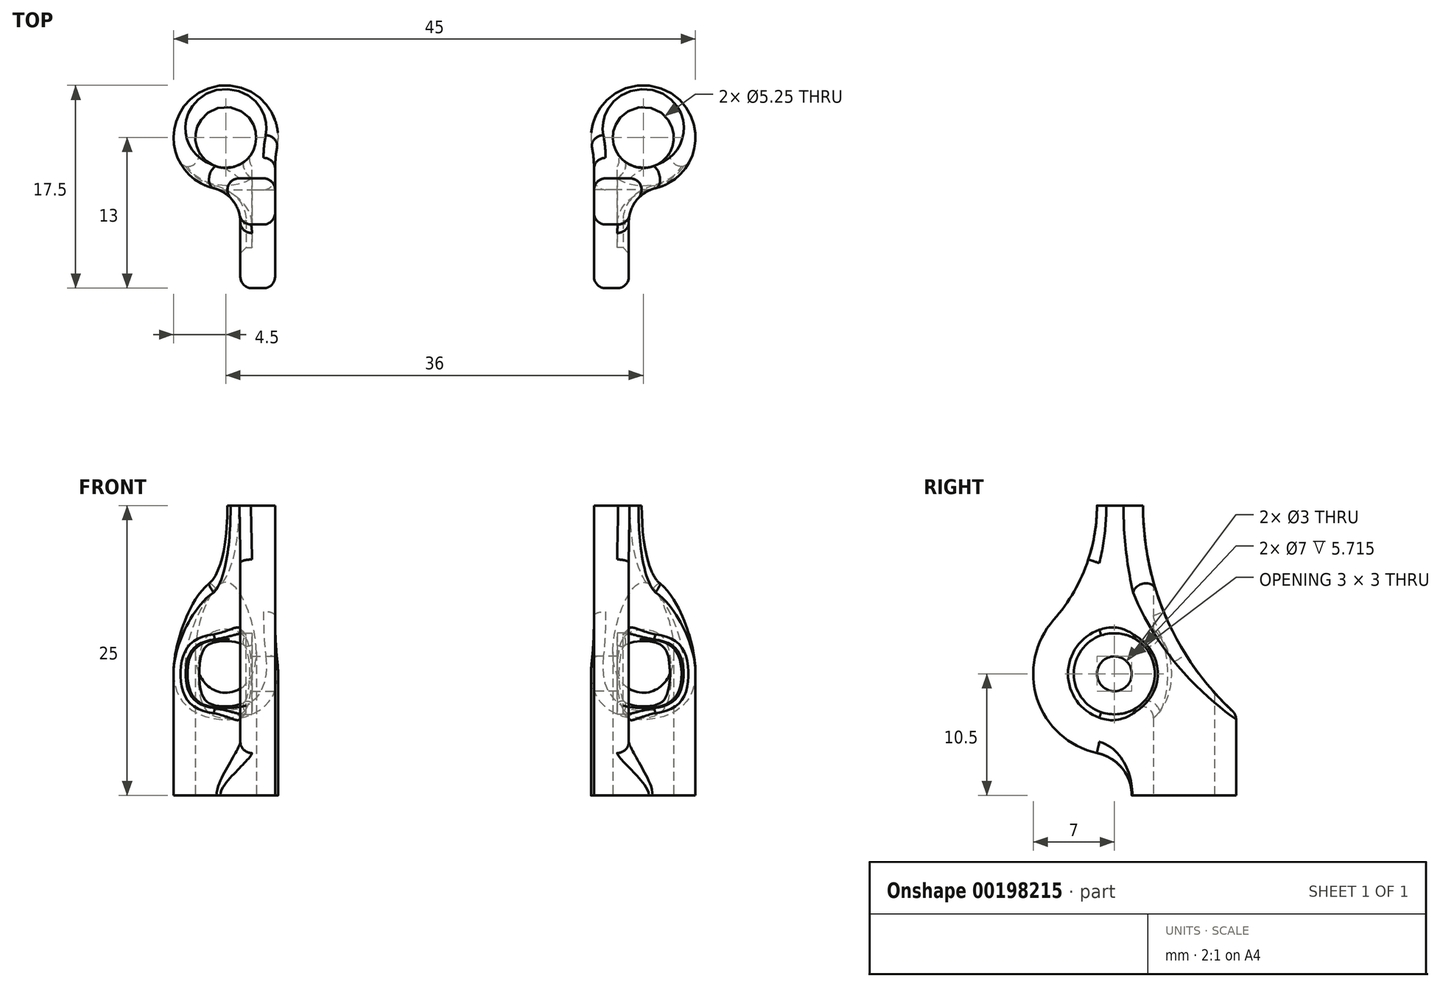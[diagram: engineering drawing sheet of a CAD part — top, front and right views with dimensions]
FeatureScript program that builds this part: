
annotation { "Feature Type Name" : "Feature", "Feature Type Description" : "" }
export const myFeature = defineFeature(function(context is Context, id is Id, definition is map)
    precondition{}
    {
        {
            var Q0;
            Q0=qCreatedBy(makeId("Top.planeOp"),FACE);
            var sketch = newSketch(context, id + "F0", { "sketchPlane" : qUnion([Q0])});
            skLineSegment(sketch, "E0", {"start": v(-13.75, 33.32) * mm, "end": v(-13.75, 22.5) * mm});
            skLineSegment(sketch, "E1", {"start": v(-13.75, 22.5) * mm, "end": v(-16.75, 22.5) * mm});
            skLineSegment(sketch, "E2", {"start": v(-16.75, 22.5) * mm, "end": v(-16.75, 28.7) * mm});
            skCircle(sketch, "E3", {"center": v(-18, 36) * mm, "radius": 2.62 * mm});
            skArc(sketch, "E4", {"start": v(-13.58, 35.17) * mm, "mid": v(-20.45, 39.78) * mm, "end": v(-19.05, 31.62) * mm});
            skPoint(sketch, "E5.visualSharp", {"position": v(-13.75, 34.52) * mm});
            skArc(sketch, "E5.filletArc", {"start": v(-13.58, 35.17) * mm, "mid": v(-13.7, 34.25) * mm, "end": v(-13.75, 33.32) * mm});
            skPoint(sketch, "E6.visualSharp", {"position": v(-16.75, 31.68) * mm});
            skArc(sketch, "E6.filletArc", {"start": v(-16.75, 28.7) * mm, "mid": v(-17.4, 30.56) * mm, "end": v(-19.05, 31.62) * mm});
            skSolve(sketch);
        }
        {
            var Q0;
            Q0=qSketchRegion(id+"F0",true);
            extrude(context, id + "F1", {"entities" : qUnion([Q0]), "depth" : 25 * mm});
        }
        {
            var Q0;
            Q0=makeQuery(id+"F1.opExtrude","SWEPT_FACE",FACE,{"disambiguationData":[OSD([sQuery(id+"F0.wireOp",EDGE,"E0")])]});
            var sketch = newSketch(context, id + "F2", { "sketchPlane" : qUnion([Q0])});
            skCircle(sketch, "E7", {"center": v(30, 10.5) * mm, "radius": 1.5 * mm});
            skArc(sketch, "E8", {"start": v(32.5, 26) * mm, "mid": v(34.36, 15.6) * mm, "end": v(40.5, 7) * mm});
            skLineSegment(sketch, "E9", {"start": v(32.5, 26) * mm, "end": v(40.5, 26) * mm});
            skLineSegment(sketch, "E10", {"start": v(40.5, 26) * mm, "end": v(40.5, 7) * mm});
            skLineSegment(sketch, "E11", {"start": v(28.5, 30) * mm, "end": v(28.5, 25) * mm});
            skArc(sketch, "E12", {"start": v(24.76, 15.14) * mm, "mid": v(27.53, 19.73) * mm, "end": v(28.5, 25) * mm});
            skArc(sketch, "E13", {"start": v(24.76, 15.14) * mm, "mid": v(23.35, 8.31) * mm, "end": v(28.54, 3.65) * mm});
            skLineSegment(sketch, "E14", {"start": v(28.5, 30) * mm, "end": v(18.5, 30) * mm});
            skLineSegment(sketch, "E15", {"start": v(18.5, 30) * mm, "end": v(18.5, -2) * mm});
            skArc(sketch, "E16", {"start": v(31.5, 0) * mm, "mid": v(30.67, 2.35) * mm, "end": v(28.54, 3.65) * mm});
            skLineSegment(sketch, "E17", {"start": v(31.5, 0) * mm, "end": v(31.5, -2) * mm});
            skLineSegment(sketch, "E18", {"start": v(31.5, -2) * mm, "end": v(18.5, -2) * mm});
            skSolve(sketch);
        }
        {
            var Q0;
            Q0=qSketchRegion(id+"F2",true);
            extrude(context, id + "F3", {"entities" : qUnion([Q0]), "operationType" : NewBodyOperationType.REMOVE, "oppositeDirection" : true, "depth" : 25 * mm, "hasSecondDirection" : true, "secondDirectionOppositeDirection" : false, "secondDirectionDepth" : 25 * mm});
        }
        {
            var Q0;
            Q0=makeQuery(id+"F1.opExtrude","SWEPT_FACE",FACE,{"disambiguationData":[OSD([sQuery(id+"F0.wireOp",EDGE,"E2")])]});
            var sketch = newSketch(context, id + "F4", { "sketchPlane" : qUnion([Q0])});
            skCircle(sketch, "E19", {"center": v(-30, 10.5) * mm, "radius": 3.5 * mm});
            skSolve(sketch);
        }
        {
            var Q0;
            Q0=qSketchRegion(id+"F4",true);
            extrude(context, id + "F5", {"entities" : qUnion([Q0]), "operationType" : NewBodyOperationType.REMOVE, "depth" : 6 * mm, "hasSecondDirection" : true, "secondDirectionOppositeDirection" : true, "secondDirectionDepth" : 1 * mm});
        }
        {
            var Q0;
            Q0=makeQuery(id+"F5.boolean.opBoolean","INTERSECT",EDGE,{"derivedFrom":[makeQuery(id+"F1.opExtrude","SWEPT_FACE",FACE,{"disambiguationData":[OSD([sQuery(id+"F0.wireOp",EDGE,"E2")])]}),makeQuery(id+"F5.opExtrude","SWEPT_FACE",FACE,{"disambiguationData":[OSD([sQuery(id+"F4.wireOp",EDGE,"E19")])]})]});
            chamfer(context, id + "F6", {"entities" : qUnion([Q0]), "width" : 0.5 * mm, "tangentPropagation" : true});
        }
        {
            var Q0;
            Q0=makeQuery(id+"F3.boolean.opBoolean","INTERSECT",EDGE,{"derivedFrom":[makeQuery(id+"F1.opExtrude","SWEPT_FACE",FACE,{"disambiguationData":[OSD([sQuery(id+"F0.wireOp",EDGE,"E2")])]}),makeQuery(id+"F3.opExtrude","SWEPT_FACE",FACE,{"disambiguationData":[OSD([sQuery(id+"F2.wireOp",EDGE,"E12")])]})]});
            var Q1;
            Q1=makeQuery(id+"F3.boolean.opBoolean","INTERSECT",EDGE,{"derivedFrom":[makeQuery(id+"F1.opExtrude","SWEPT_FACE",FACE,{"disambiguationData":[OSD([sQuery(id+"F0.wireOp",EDGE,"E0")])]}),makeQuery(id+"F3.opExtrude","SWEPT_FACE",FACE,{"disambiguationData":[OSD([sQuery(id+"F2.wireOp",EDGE,"E12")])]})]});
            var Q2;
            Q2=makeQuery(id+"F3.boolean.opBoolean","INTERSECT",EDGE,{"derivedFrom":[makeQuery(id+"F1.opExtrude","SWEPT_FACE",FACE,{"disambiguationData":[OSD([sQuery(id+"F0.wireOp",EDGE,"E4")])]}),makeQuery(id+"F3.opExtrude","SWEPT_FACE",FACE,{"disambiguationData":[OSD([sQuery(id+"F2.wireOp",EDGE,"E8")])]})]});
            var Q3;
            Q3=makeQuery(id+"F5.boolean.opBoolean","INTERSECT",EDGE,{"derivedFrom":[makeQuery(id+"F1.opExtrude","SWEPT_FACE",FACE,{"disambiguationData":[OSD([sQuery(id+"F0.wireOp",EDGE,"E3")])]}),makeQuery(id+"F5.opExtrude","SWEPT_FACE",FACE,{"disambiguationData":[OSD([sQuery(id+"F4.wireOp",EDGE,"E19")])]})]});
            fillet(context, id + "F7", {"entities" : qUnion([Q0, Q1, Q2, Q3]), "radius" : 1 * mm, "tangentPropagation" : true, "allowEdgeOverflow" : false});
        }
        {
            var Q0;
            Q0=makeQuery(id+"F1.opExtrude","SWEPT_BODY",BODY,{"disambiguationData":[OSD([sQuery(id+"F0.wireOp",EDGE,"E0"),sQuery(id+"F0.wireOp",EDGE,"E1"),sQuery(id+"F0.wireOp",EDGE,"E2"),sQuery(id+"F0.wireOp",EDGE,"E3"),sQuery(id+"F0.wireOp",EDGE,"E4"),sQuery(id+"F0.wireOp",EDGE,"E5.filletArc"),sQuery(id+"F0.wireOp",EDGE,"E6.filletArc")])]});
            var Q1;
            Q1=qCreatedBy(makeId("Right.planeOp"),FACE);
            mirror(context, id + "F8", {"entities" : qUnion([Q0]), "mirrorPlane" : qUnion([Q1])});
        }
    });
